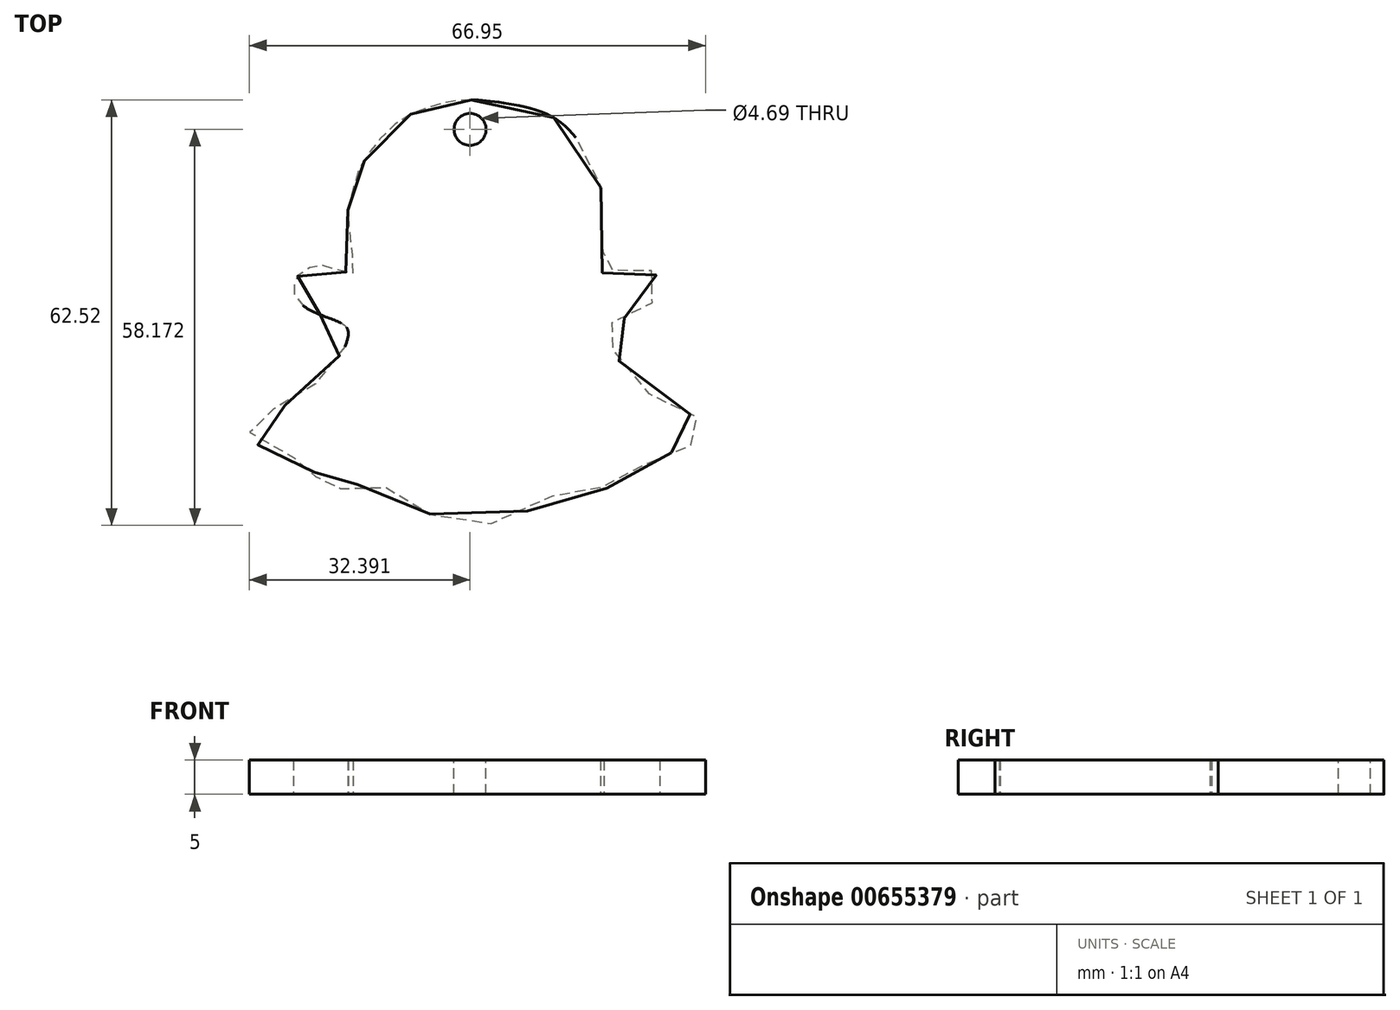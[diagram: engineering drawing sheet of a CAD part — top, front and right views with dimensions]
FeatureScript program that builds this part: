
annotation { "Feature Type Name" : "Feature", "Feature Type Description" : "" }
export const myFeature = defineFeature(function(context is Context, id is Id, definition is map)
    precondition{}
    {
        {
            var Q0;
            Q0=qCreatedBy(makeId("Top.planeOp"),FACE);
            var sketch = newSketch(context, id + "F0", { "sketchPlane" : qUnion([Q0])});
            skFitSpline(sketch, "E0", {"points": [v(-37.13, 67.7) * mm, v(-40.43, 67.4) * mm, v(-43.84, 66.42) * mm, v(-47.47, 64.77) * mm, v(-51.47, 60.8) * mm, v(-52.53, 59.21) * mm, v(-53.69, 57.36) * mm, v(-54.15, 55.68) * mm, v(-55.08, 52.35) * mm, v(-55.18, 50.1) * mm, v(-54.55, 42.17) * mm, v(-54.87, 42.33) * mm, v(-56.08, 42.43) * mm, v(-58.28, 43.27) * mm, v(-60.7, 43.11) * mm, v(-62.79, 41.6) * mm, v(-63.16, 40.6) * mm, v(-63, 38.81) * mm, v(-60.27, 36.56) * mm, v(-56.29, 34.93) * mm, v(-55.2, 33.7) * mm, v(-56.24, 30.44) * mm, v(-59.36, 26.73) * mm, v(-62.92, 23.46) * mm, v(-67.97, 21.68) * mm, v(-69.6, 20.2) * mm, v(-68.56, 17.08) * mm, v(-62.33, 15) * mm, v(-61, 14.7) * mm, v(-60.06, 12.53) * mm, v(-59.4, 10.95) * mm, v(-56.97, 10.48) * mm, v(-53.51, 11.23) * mm, v(-48, 10.1) * mm, v(-43.14, 6.83) * mm, v(-35.75, 5.24) * mm, v(-26.22, 8.8) * mm, v(-21.73, 11.32) * mm, v(-14.91, 10.76) * mm, v(-12.01, 14.12) * mm, v(-5.94, 16.46) * mm, v(-2.76, 19.26) * mm, v(-3.79, 20.95) * mm, v(-7.9, 22.54) * mm, v(-14.54, 27.96) * mm, v(-16.87, 32.07) * mm, v(-17.62, 34.13) * mm, v(-15.2, 35.43) * mm, v(-11.17, 37.4) * mm, v(-9.49, 39.83) * mm, v(-10.24, 42.26) * mm, v(-13.5, 43.38) * mm, v(-16.6, 42.54) * mm, v(-18, 42.35) * mm, v(-17.9, 44.5) * mm, v(-18, 54.22) * mm, v(-19.96, 59.55) * mm, v(-25, 65.06) * mm, v(-32.76, 67.3) * mm, v(-37.13, 67.7) * mm]});
            skSolve(sketch);
        }
        {
            var Q0;
            Q0 = qSketchRegion(id + "F0", true);
            extrude(context, id + "F1", {"entities" : qUnion([Q0]), "depth" : 5 * mm, "offsetDistance" : 25.4 * mm});
        }
        {
            var Q0;
            Q0=makeQuery(id+"F1.opExtrude","CAP_FACE",FACE,{"disambiguationData":[OSD([sQuery(id+"F0.wireOp",EDGE,"E0")])],"isStart":false});
            var sketch = newSketch(context, id + "F2", { "sketchPlane" : qUnion([Q0])});
            skCircle(sketch, "E1", {"center": v(-37.3, 63.36) * mm, "radius": 2.35 * mm});
            skSolve(sketch);
        }
        {
            var Q0;
            Q0 = qSketchRegion(id + "F2", true);
            extrude(context, id + "F3", {"entities" : qUnion([Q0]), "operationType" : NewBodyOperationType.REMOVE, "oppositeDirection" : true, "depth" : 5 * mm, "offsetDistance" : 25 * mm});
        }
    });
